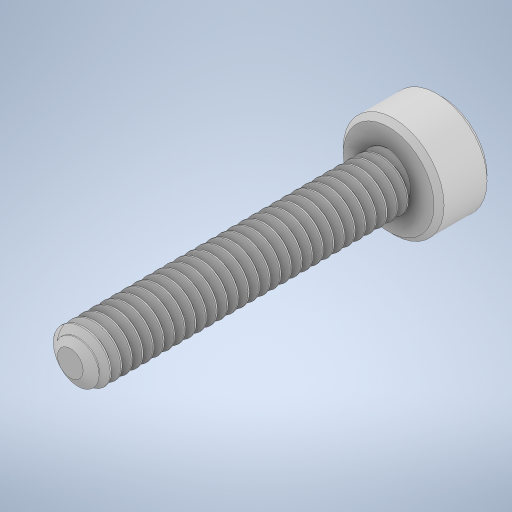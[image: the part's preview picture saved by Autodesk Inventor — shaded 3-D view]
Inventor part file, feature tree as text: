
AUTODESK INVENTOR PART (.ipt)
format: ipt  version: 2024 (Build 280153000, 153)  size: 1,008,640 bytes
history: native  units: mm
features: other x1, chamfer x1
ambient origin geometry x8: Origin, YZ Plane, XZ Plane, XY Plane, X Axis, Y Axis, Z Axis, Center Point
bodies: Body1 (feature_tree)
feature tree (2):
  other  "Těleso1"
  chamfer  "Chamfer1"  [1 undecoded]
note: 1 required parameter value undecoded (feature->parameter linkage not recoverable at this tier; creation-order binding heuristic only, values carry confidence <= 0.55)
